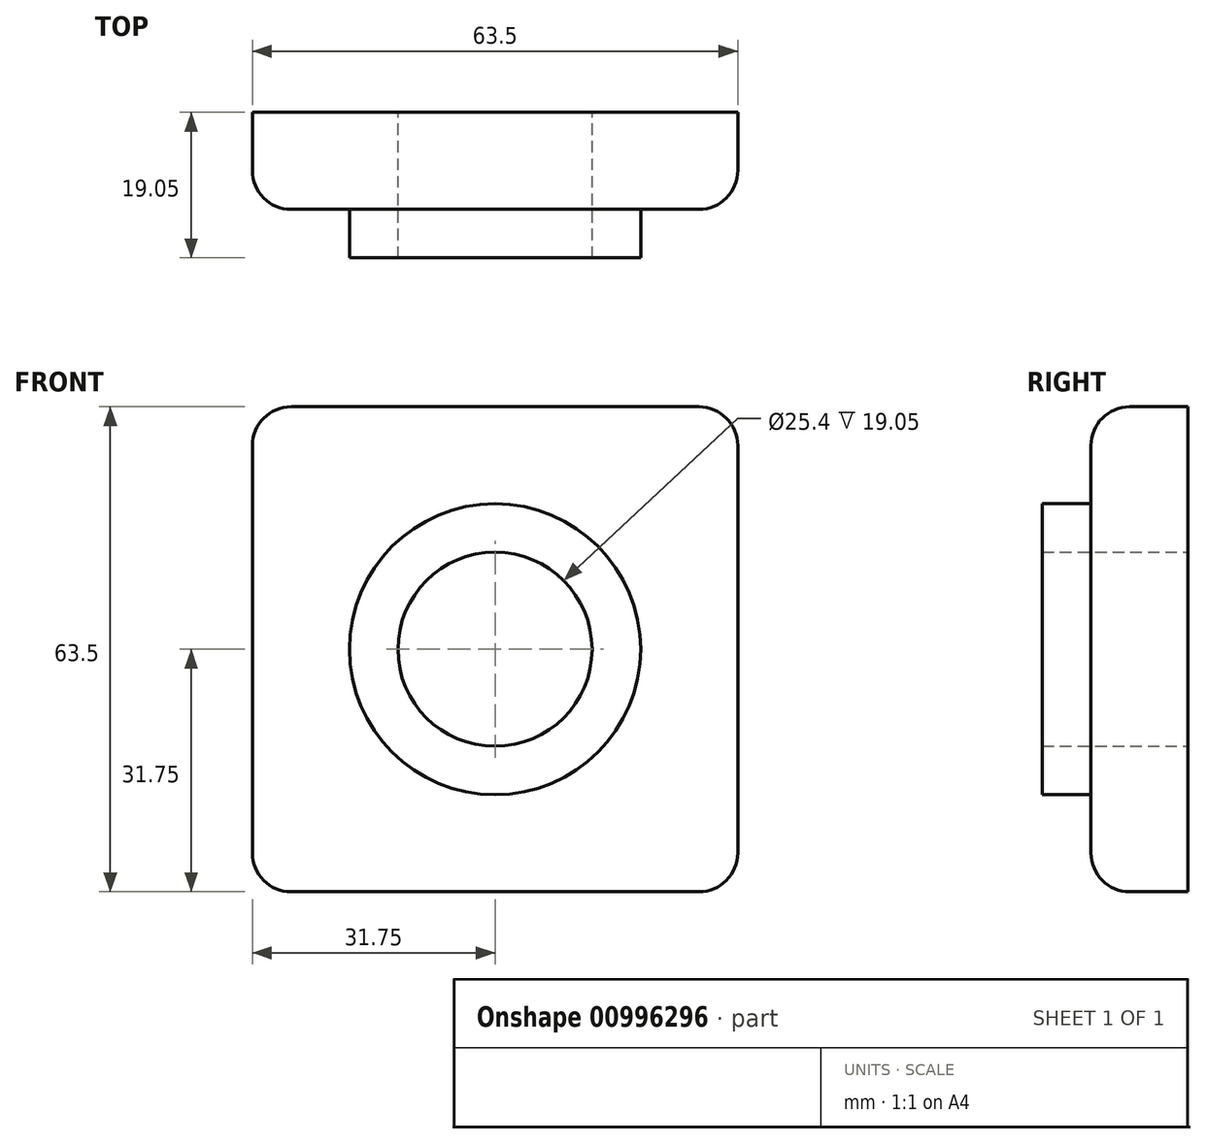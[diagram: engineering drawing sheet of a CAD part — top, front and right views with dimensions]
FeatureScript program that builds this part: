
annotation { "Feature Type Name" : "Feature", "Feature Type Description" : "" }
export const myFeature = defineFeature(function(context is Context, id is Id, definition is map)
    precondition{}
    {
        {
            var Q0;
            Q0=qCreatedBy(makeId("Front.planeOp"),FACE);
            var sketch = newSketch(context, id + "F0", { "sketchPlane" : qUnion([Q0])});
            skCircle(sketch, "E0", {"center": v(0, 0) * mm, "radius": 12.7 * mm});
            skCircle(sketch, "E1", {"center": v(0, 0) * mm, "radius": 19.05 * mm});
            skLineSegment(sketch, "E2", {"start": v(0, 0) * mm, "end": v(0, 31.75) * mm});
            skLineSegment(sketch, "E3", {"start": v(0, 31.75) * mm, "end": v(-31.75, 31.75) * mm});
            skLineSegment(sketch, "E4", {"start": v(-31.75, 31.75) * mm, "end": v(0, 0) * mm});
            skLineSegment(sketch, "E5.bottom", {"start": v(-31.75, 31.75) * mm, "end": v(31.75, 31.75) * mm});
            skLineSegment(sketch, "E5.top", {"start": v(-31.75, -31.75) * mm, "end": v(31.75, -31.75) * mm});
            skLineSegment(sketch, "E5.left", {"start": v(-31.75, 31.75) * mm, "end": v(-31.75, -31.75) * mm});
            skLineSegment(sketch, "E5.right", {"start": v(31.75, 31.75) * mm, "end": v(31.75, -31.75) * mm});
            skSolve(sketch);
        }
        {
            var Q0;
            Q0=makeQuery(id+"F0.imprint","IMPRINT",FACE,{"disambiguationData":[TD([[makeQuery(id+"F0.imprint","IMPRINT",EDGE,{"derivedFrom":sQuery(id+"F0.wireOp",EDGE,"E5.top")}),1.0]])]});
            var Q1;
            {var subQ0=sQuery(id+"F0.wireOp",EDGE,"E2");var subQ1=sQuery(id+"F0.wireOp",EDGE,"E1");var subQ2=makeQuery(id+"F0.imprint","INTERSECT",VERTEX,{"derivedFrom":[subQ1,subQ0]});Q1=makeQuery(id+"F0.imprint","IMPRINT",FACE,{"disambiguationData":[TD([[makeQuery(id+"F0.imprint","IMPRINT",EDGE,{"disambiguationData":[TD([[subQ2,-1.0]])],"derivedFrom":subQ1}),-1.0]])]});}
            extrude(context, id + "F1", {"entities" : qUnion([Q0, Q1]), "depth" : 12.7 * mm, "offsetDistance" : 25.4 * mm});
        }
        {
            var Q0;
            Q0=qCreatedBy(makeId("Front.planeOp"),FACE);
            var sketch = newSketch(context, id + "F2", { "sketchPlane" : qUnion([Q0])});
            skCircle(sketch, "E6", {"center": v(0, 0) * mm, "radius": 19.05 * mm});
            skCircle(sketch, "E7", {"center": v(0, 0) * mm, "radius": 12.7 * mm});
            skSolve(sketch);
        }
        {
            var Q0;
            Q0=makeQuery(id+"F2.imprint","IMPRINT",FACE,{"disambiguationData":[TD([[makeQuery(id+"F2.imprint","IMPRINT",EDGE,{"derivedFrom":sQuery(id+"F2.wireOp",EDGE,"E6")}),1.0]])]});
            extrude(context, id + "F3", {"entities" : qUnion([Q0]), "operationType" : NewBodyOperationType.ADD, "depth" : 19.05 * mm, "offsetDistance" : 25.4 * mm});
        }
        {
            var Q0;
            Q0=makeQuery(id+"F1.opExtrude","CAP_EDGE",EDGE,{"disambiguationData":[OSD([sQuery(id+"F0.wireOp",EDGE,"E1")])],"isStart":false});
            var Q1;
            Q1=makeQuery(id+"F1.opExtrude","CAP_EDGE",EDGE,{"disambiguationData":[OSD([sQuery(id+"F0.wireOp",EDGE,"E5.bottom")])],"isStart":false});
            var Q2;
            Q2=makeQuery(id+"F1.opExtrude","CAP_EDGE",EDGE,{"disambiguationData":[OSD([sQuery(id+"F0.wireOp",EDGE,"E5.left")])],"isStart":false});
            var Q3;
            Q3=makeQuery(id+"F1.opExtrude","CAP_EDGE",EDGE,{"disambiguationData":[OSD([sQuery(id+"F0.wireOp",EDGE,"E5.top")])],"isStart":false});
            var Q4;
            Q4=makeQuery(id+"F1.opExtrude","CAP_EDGE",EDGE,{"disambiguationData":[OSD([sQuery(id+"F0.wireOp",EDGE,"E5.right")])],"isStart":false});
            var Q5;
            Q5=makeQuery(id+"F1.opExtrude","SWEPT_EDGE",EDGE,{"disambiguationData":[OSD([sQuery(id+"F0.wireOp",EDGE,"E5.bottom"),sQuery(id+"F0.wireOp",EDGE,"E5.right")])]});
            var Q6;
            Q6=makeQuery(id+"F1.opExtrude","SWEPT_EDGE",EDGE,{"disambiguationData":[OSD([sQuery(id+"F0.wireOp",EDGE,"E4"),sQuery(id+"F0.wireOp",EDGE,"E5.bottom"),sQuery(id+"F0.wireOp",EDGE,"E5.left")])]});
            var Q7;
            Q7=makeQuery(id+"F1.opExtrude","SWEPT_EDGE",EDGE,{"disambiguationData":[OSD([sQuery(id+"F0.wireOp",EDGE,"E5.top"),sQuery(id+"F0.wireOp",EDGE,"E5.left")])]});
            var Q8;
            Q8=makeQuery(id+"F1.opExtrude","SWEPT_EDGE",EDGE,{"disambiguationData":[OSD([sQuery(id+"F0.wireOp",EDGE,"E5.top"),sQuery(id+"F0.wireOp",EDGE,"E5.right")])]});
            fillet(context, id + "F4", {"entities" : qUnion([Q0, Q1, Q2, Q3, Q4, Q5, Q6, Q7, Q8]), "radius" : 5.08 * mm, "tangentPropagation" : true, "allowEdgeOverflow" : false});
        }
    });
